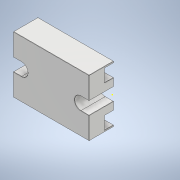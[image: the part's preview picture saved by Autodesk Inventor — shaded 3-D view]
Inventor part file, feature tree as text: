
AUTODESK INVENTOR PART (.ipt)
format: ipt  version: 2020 (Build 240168000, 168)  size: 286,720 bytes
history: native  units: mm
features: extrude x4, thread x4, other x3, sketch x2, fillet x1, hole x1
ambient origin geometry x8: Origin, YZ Plane, XZ Plane, XY Plane, X Axis, Y Axis, Z Axis, Center Point
bodies: Body1 (feature_tree)
feature tree (15):
  other  "SSR-XXDA"
  other  "Твердое тело1"
  extrude  "Выдавливание1"  Depth=80.0mm
  sketch  "Эскиз2"
  extrude  "Выдавливание2"  Depth=19.5mm TaperAngle=0.0deg
  extrude  "Выдавливание3"  Depth=5.0mm
  extrude  "Выдавливание4"  Depth=6.5mm
  fillet  "Сопряжение1"  Radius=10.0mm
  hole  "Отверстие1"  [1 undecoded]
  thread  "Резьба1"
  thread  "Резьба2"
  thread  "Резьба3"
  thread  "Резьба4"
  sketch  "Эскиз1"
  other  "Картинка1"
note: 1 required parameter value undecoded (feature->parameter linkage not recoverable at this tier; creation-order binding heuristic only, values carry confidence <= 0.55)
